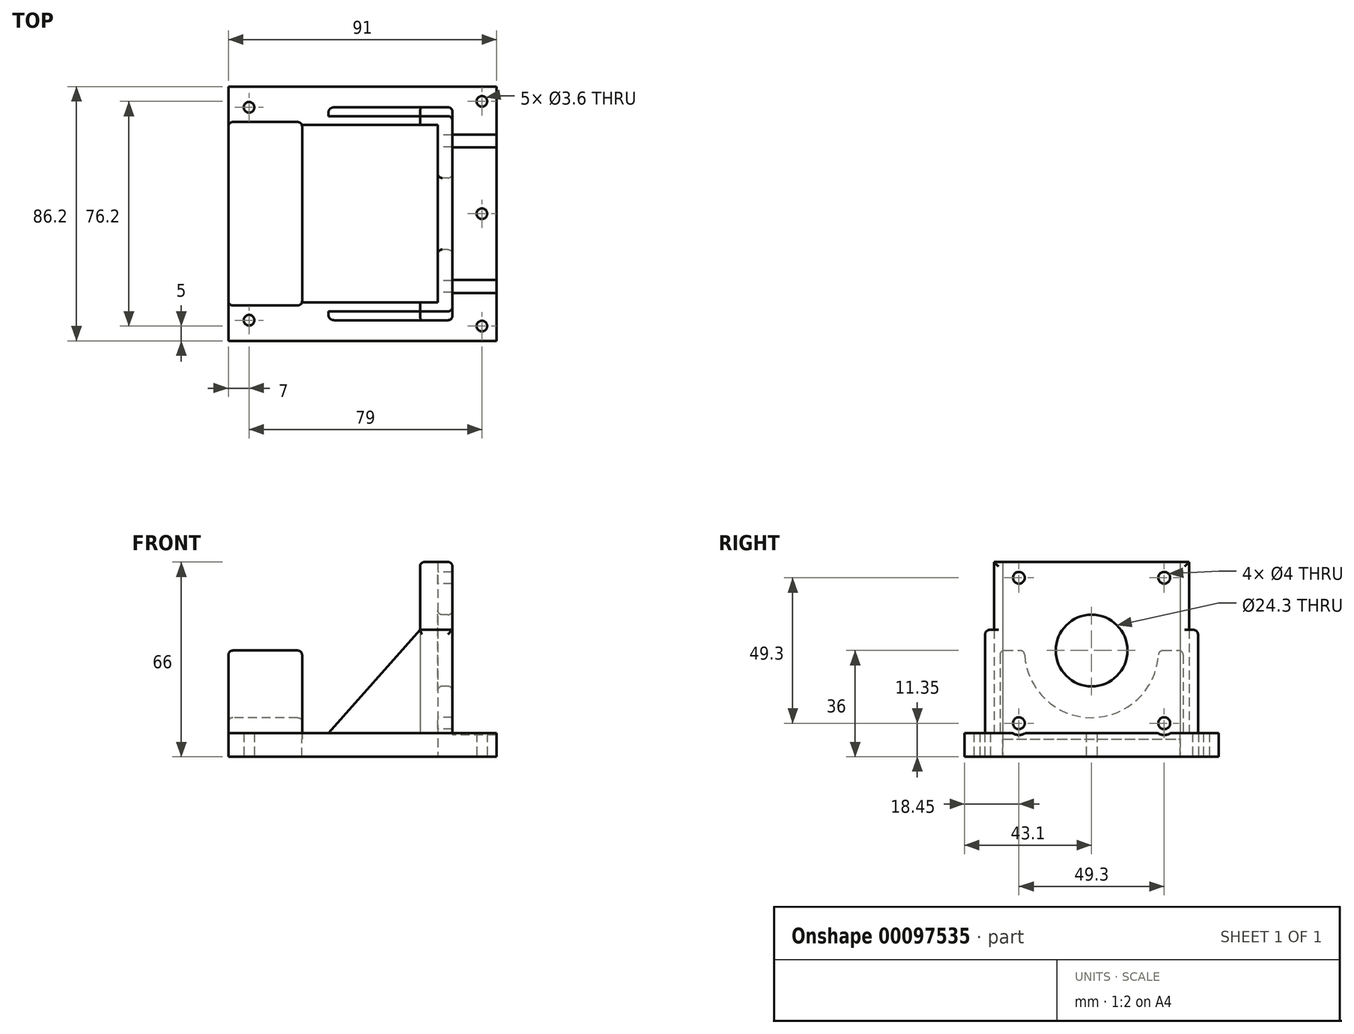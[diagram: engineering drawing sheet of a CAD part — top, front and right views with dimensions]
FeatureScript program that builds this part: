
annotation { "Feature Type Name" : "Feature", "Feature Type Description" : "" }
export const myFeature = defineFeature(function(context is Context, id is Id, definition is map)
    precondition{}
    {
        {
            var Q0;
            Q0=qCreatedBy(makeId("Right.planeOp"),FACE);
            var sketch = newSketch(context, id + "F0", { "sketchPlane" : qUnion([Q0])});
            skLineSegment(sketch, "E0.bottom", {"start": v(-30.1, 60) * mm, "end": v(30.1, 60) * mm});
            skLineSegment(sketch, "E0.top", {"start": v(-30.1, 0) * mm, "end": v(30.1, 0) * mm});
            skLineSegment(sketch, "E0.left", {"start": v(-30.1, 60) * mm, "end": v(-30.1, 0) * mm});
            skLineSegment(sketch, "E0.right", {"start": v(30.1, 60) * mm, "end": v(30.1, 0) * mm});
            skLineSegment(sketch, "E1.bottom", {"start": v(-33.1, 63) * mm, "end": v(33.1, 63) * mm});
            skLineSegment(sketch, "E1.top", {"start": v(-33.1, 0) * mm, "end": v(33.1, 0) * mm});
            skLineSegment(sketch, "E1.left", {"start": v(-33.1, 63) * mm, "end": v(-33.1, 0) * mm});
            skLineSegment(sketch, "E1.right", {"start": v(33.1, 63) * mm, "end": v(33.1, 0) * mm});
            skCircle(sketch, "E2", {"center": v(-24.65, 54.65) * mm, "radius": 2 * mm});
            skCircle(sketch, "E3", {"center": v(24.65, 54.65) * mm, "radius": 2 * mm});
            skCircle(sketch, "E4", {"center": v(24.65, 5.35) * mm, "radius": 2 * mm});
            skCircle(sketch, "E5", {"center": v(-24.65, 5.35) * mm, "radius": 2 * mm});
            skCircle(sketch, "E6", {"center": v(0, 30) * mm, "radius": 12.15 * mm});
            skSolve(sketch);
        }
        {
            var Q0;
            Q0=makeQuery(id+"F0.imprint","IMPRINT",FACE,{"disambiguationData":[TD([[makeQuery(id+"F0.imprint","IMPRINT",EDGE,{"derivedFrom":sQuery(id+"F0.wireOp",EDGE,"E0.bottom")}),1.0]])]});
            var Q1;
            Q1=makeQuery(id+"F0.imprint","IMPRINT",FACE,{"disambiguationData":[TD([[makeQuery(id+"F0.imprint","IMPRINT",EDGE,{"derivedFrom":sQuery(id+"F0.wireOp",EDGE,"E0.bottom")}),-1.0]])]});
            extrude(context, id + "F1", {"entities" : qUnion([Q0, Q1]), "depth" : 5 * mm});
        }
        {
            var Q0;
            Q0=makeQuery(id+"F0.imprint","IMPRINT",FACE,{"disambiguationData":[TD([[makeQuery(id+"F0.imprint","IMPRINT",EDGE,{"derivedFrom":sQuery(id+"F0.wireOp",EDGE,"E0.bottom")}),1.0]])]});
            extrude(context, id + "F2", {"entities" : qUnion([Q0]), "operationType" : NewBodyOperationType.ADD, "oppositeDirection" : true, "depth" : 6 * mm});
        }
        {
            var Q0;
            Q0=qCreatedBy(makeId("Top.planeOp"),FACE);
            var sketch = newSketch(context, id + "F3", { "sketchPlane" : qUnion([Q0])});
            skLineSegment(sketch, "E7.bottom", {"start": v(-6, -43.1) * mm, "end": v(20, -43.1) * mm});
            skLineSegment(sketch, "E7.top", {"start": v(-6, 43.1) * mm, "end": v(20, 43.1) * mm});
            skLineSegment(sketch, "E7.left", {"start": v(-6, -43.1) * mm, "end": v(-6, -30.1) * mm});
            skLineSegment(sketch, "E7.right", {"start": v(20, -43.1) * mm, "end": v(20, 43.1) * mm});
            skLineSegment(sketch, "E8.bottom", {"start": v(0, -30.1) * mm, "end": v(-6, -30.1) * mm});
            skLineSegment(sketch, "E8.top", {"start": v(0, 30.1) * mm, "end": v(-6, 30.1) * mm});
            skLineSegment(sketch, "E8.left", {"start": v(0, -30.1) * mm, "end": v(0, 30.1) * mm});
            skLineSegment(sketch, "E9.trimOffspring", {"start": v(-6, 30.1) * mm, "end": v(-6, 43.1) * mm});
            skCircle(sketch, "E10", {"center": v(15, -38.1) * mm, "radius": 1.8 * mm});
            skCircle(sketch, "E11", {"center": v(15, 38.1) * mm, "radius": 1.8 * mm});
            skCircle(sketch, "E12", {"center": v(15, 0) * mm, "radius": 1.8 * mm});
            skSolve(sketch);
        }
        {
            var Q0;
            Q0=makeQuery(id+"F3.imprint","IMPRINT",FACE,{"disambiguationData":[TD([[makeQuery(id+"F3.imprint","IMPRINT",EDGE,{"derivedFrom":sQuery(id+"F3.wireOp",EDGE,"E7.bottom")}),1.0]])]});
            extrude(context, id + "F4", {"entities" : qUnion([Q0]), "operationType" : NewBodyOperationType.ADD, "depth" : 2 * mm});
        }
        {
            var Q0;
            Q0=makeQuery(id+"F1.opExtrude","CAP_FACE",FACE,{"disambiguationData":[OSD([sQuery(id+"F0.wireOp",EDGE,"E1.bottom"),sQuery(id+"F0.wireOp",EDGE,"E1.top"),sQuery(id+"F0.wireOp",EDGE,"E1.left"),sQuery(id+"F0.wireOp",EDGE,"E1.right"),sQuery(id+"F0.wireOp",EDGE,"E2"),sQuery(id+"F0.wireOp",EDGE,"E3"),sQuery(id+"F0.wireOp",EDGE,"E4"),sQuery(id+"F0.wireOp",EDGE,"E5"),sQuery(id+"F0.wireOp",EDGE,"E6")])],"isStart":false});
            var sketch = newSketch(context, id + "F5", { "sketchPlane" : qUnion([Q0])});
            skCircle(sketch, "E13", {"center": v(-24.65, 5.35) * mm, "radius": 4 * mm});
            skCircle(sketch, "E14", {"center": v(24.65, 5.35) * mm, "radius": 4 * mm});
            skSolve(sketch);
        }
        {
            var Q0;
            {var subQ1=sQuery(id+"F0.wireOp",EDGE,"E5");Q0=makeQuery(id+"F5.imprint","IMPRINT",FACE,{"disambiguationData":[TD([[makeQuery(id+"F5.imprint","IMPRINT",EDGE,{"derivedFrom":makeQuery(id+"F1.opExtrude","CAP_EDGE",EDGE,{"disambiguationData":[OSD([subQ1])],"isStart":false})}),-1.0]])]});}
            var Q1;
            {var subQ0=sQuery(id+"F5.wireOp",EDGE,"E13");var subQ1=makeQuery(id+"F4.boolean.opBoolean","INTERSECT",EDGE,{"derivedFrom":[makeQuery(id+"F1.opExtrude","CAP_FACE",FACE,{"disambiguationData":[OSD([sQuery(id+"F0.wireOp",EDGE,"E1.bottom"),sQuery(id+"F0.wireOp",EDGE,"E1.top"),sQuery(id+"F0.wireOp",EDGE,"E1.left"),sQuery(id+"F0.wireOp",EDGE,"E1.right"),sQuery(id+"F0.wireOp",EDGE,"E2"),sQuery(id+"F0.wireOp",EDGE,"E3"),sQuery(id+"F0.wireOp",EDGE,"E4"),sQuery(id+"F0.wireOp",EDGE,"E5"),sQuery(id+"F0.wireOp",EDGE,"E6")])],"isStart":false}),makeQuery(id+"F4.opExtrude","CAP_FACE",FACE,{"disambiguationData":[OSD([sQuery(id+"F3.wireOp",EDGE,"E7.bottom"),sQuery(id+"F3.wireOp",EDGE,"E7.top"),sQuery(id+"F3.wireOp",EDGE,"E7.left"),sQuery(id+"F3.wireOp",EDGE,"E7.right"),sQuery(id+"F3.wireOp",EDGE,"E8.bottom"),sQuery(id+"F3.wireOp",EDGE,"E8.top"),sQuery(id+"F3.wireOp",EDGE,"E8.left"),sQuery(id+"F3.wireOp",EDGE,"E9.trimOffspring"),sQuery(id+"F3.wireOp",EDGE,"E10"),sQuery(id+"F3.wireOp",EDGE,"E11"),sQuery(id+"F3.wireOp",EDGE,"vc0lLMzM-xdFk-joIx-QcfE-IC59JL1JUAtQ"),sQuery(id+"F3.wireOp",EDGE,"XxfvqPpx-BB1E-VwMp-cwxA-6DKMUQReIGj5")])],"isStart":false})]});var subQ2=makeQuery(id+"F5.imprint","INTERSECT",VERTEX,{"disambiguationData":[OD(0.0)],"derivedFrom":[subQ1,subQ0]});Q1=makeQuery(id+"F5.imprint","IMPRINT",FACE,{"disambiguationData":[TD([[makeQuery(id+"F5.imprint","IMPRINT",EDGE,{"disambiguationData":[TD([[subQ2,-1.0]])],"derivedFrom":subQ0}),1.0]])]});}
            var Q2;
            {var subQ1=sQuery(id+"F0.wireOp",EDGE,"E4");Q2=makeQuery(id+"F5.imprint","IMPRINT",FACE,{"disambiguationData":[TD([[makeQuery(id+"F5.imprint","IMPRINT",EDGE,{"derivedFrom":makeQuery(id+"F1.opExtrude","CAP_EDGE",EDGE,{"disambiguationData":[OSD([subQ1])],"isStart":false})}),-1.0]])]});}
            var Q3;
            {var subQ0=sQuery(id+"F5.wireOp",EDGE,"E14");var subQ1=makeQuery(id+"F4.boolean.opBoolean","INTERSECT",EDGE,{"derivedFrom":[makeQuery(id+"F1.opExtrude","CAP_FACE",FACE,{"disambiguationData":[OSD([sQuery(id+"F0.wireOp",EDGE,"E1.bottom"),sQuery(id+"F0.wireOp",EDGE,"E1.top"),sQuery(id+"F0.wireOp",EDGE,"E1.left"),sQuery(id+"F0.wireOp",EDGE,"E1.right"),sQuery(id+"F0.wireOp",EDGE,"E2"),sQuery(id+"F0.wireOp",EDGE,"E3"),sQuery(id+"F0.wireOp",EDGE,"E4"),sQuery(id+"F0.wireOp",EDGE,"E5"),sQuery(id+"F0.wireOp",EDGE,"E6")])],"isStart":false}),makeQuery(id+"F4.opExtrude","CAP_FACE",FACE,{"disambiguationData":[OSD([sQuery(id+"F3.wireOp",EDGE,"E7.bottom"),sQuery(id+"F3.wireOp",EDGE,"E7.top"),sQuery(id+"F3.wireOp",EDGE,"E7.left"),sQuery(id+"F3.wireOp",EDGE,"E7.right"),sQuery(id+"F3.wireOp",EDGE,"E8.bottom"),sQuery(id+"F3.wireOp",EDGE,"E8.top"),sQuery(id+"F3.wireOp",EDGE,"E8.left"),sQuery(id+"F3.wireOp",EDGE,"E9.trimOffspring"),sQuery(id+"F3.wireOp",EDGE,"E10"),sQuery(id+"F3.wireOp",EDGE,"E11"),sQuery(id+"F3.wireOp",EDGE,"vc0lLMzM-xdFk-joIx-QcfE-IC59JL1JUAtQ"),sQuery(id+"F3.wireOp",EDGE,"XxfvqPpx-BB1E-VwMp-cwxA-6DKMUQReIGj5")])],"isStart":false})]});var subQ2=makeQuery(id+"F5.imprint","INTERSECT",VERTEX,{"disambiguationData":[OD(0.0)],"derivedFrom":[subQ1,subQ0]});Q3=makeQuery(id+"F5.imprint","IMPRINT",FACE,{"disambiguationData":[TD([[makeQuery(id+"F5.imprint","IMPRINT",EDGE,{"disambiguationData":[TD([[subQ2,1.0]])],"derivedFrom":subQ0}),1.0]])]});}
            var Q4;
            Q4=makeQuery(id+"F4.opExtrude","SWEPT_FACE",FACE,{"disambiguationData":[OSD([sQuery(id+"F3.wireOp",EDGE,"E7.right")])]});
            extrude(context, id + "F6", {"entities" : qUnion([Q0, Q1, Q2, Q3]), "operationType" : NewBodyOperationType.REMOVE, "endBound" : BoundingType.UP_TO_SURFACE, "endBoundEntityFace" : qUnion([Q4]), "depth" : 25 * mm});
        }
        {
            var Q0;
            Q0=qCreatedBy(makeId("Top.planeOp"),FACE);
            var sketch = newSketch(context, id + "F7", { "sketchPlane" : qUnion([Q0])});
            skLineSegment(sketch, "E15.bottom", {"start": v(-71, -43.1) * mm, "end": v(-6, -43.1) * mm});
            skLineSegment(sketch, "E15.top", {"start": v(-71, -30.1) * mm, "end": v(-6, -30.1) * mm});
            skLineSegment(sketch, "E15.left", {"start": v(-71, -43.1) * mm, "end": v(-71, -30.1) * mm});
            skLineSegment(sketch, "E15.right", {"start": v(-6, -43.1) * mm, "end": v(-6, -30.1) * mm});
            skLineSegment(sketch, "E16.bottom", {"start": v(-6, 30.1) * mm, "end": v(-71, 30.1) * mm});
            skLineSegment(sketch, "E16.top", {"start": v(-6, 43.1) * mm, "end": v(-71, 43.1) * mm});
            skLineSegment(sketch, "E16.left", {"start": v(-6, 30.1) * mm, "end": v(-6, 43.1) * mm});
            skLineSegment(sketch, "E16.right", {"start": v(-71, 30.1) * mm, "end": v(-71, 43.1) * mm});
            skCircle(sketch, "E17", {"center": v(-64, -36.1) * mm, "radius": 1.8 * mm});
            skCircle(sketch, "E18", {"center": v(-64, 36.1) * mm, "radius": 1.8 * mm});
            skSolve(sketch);
        }
        {
            var Q0;
            Q0=makeQuery(id+"F7.imprint","IMPRINT",FACE,{"disambiguationData":[TD([[makeQuery(id+"F7.imprint","IMPRINT",EDGE,{"derivedFrom":sQuery(id+"F7.wireOp",EDGE,"E15.bottom")}),1.0]])]});
            var Q1;
            Q1=makeQuery(id+"F7.imprint","IMPRINT",FACE,{"disambiguationData":[TD([[makeQuery(id+"F7.imprint","IMPRINT",EDGE,{"derivedFrom":sQuery(id+"F7.wireOp",EDGE,"E16.bottom")}),-1.0]])]});
            extrude(context, id + "F8", {"entities" : qUnion([Q0, Q1]), "operationType" : NewBodyOperationType.ADD, "depth" : 2 * mm});
        }
        {
            var Q0;
            Q0=qCreatedBy(makeId("Top.planeOp"),FACE);
            var sketch = newSketch(context, id + "F9", { "sketchPlane" : qUnion([Q0])});
            skLineSegment(sketch, "E19.bottom", {"start": v(-71, -31.1) * mm, "end": v(-46, -31.1) * mm});
            skLineSegment(sketch, "E19.top", {"start": v(-71, 31.1) * mm, "end": v(-46, 31.1) * mm});
            skLineSegment(sketch, "E19.left", {"start": v(-71, -31.1) * mm, "end": v(-71, 31.1) * mm});
            skLineSegment(sketch, "E19.right", {"start": v(-46, -31.1) * mm, "end": v(-46, 31.1) * mm});
            skSolve(sketch);
        }
        {
            var Q0;
            Q0=makeQuery(id+"F9.imprint","IMPRINT",FACE,{"disambiguationData":[TD([[makeQuery(id+"F9.imprint","IMPRINT",EDGE,{"derivedFrom":sQuery(id+"F9.wireOp",EDGE,"E19.bottom")}),1.0]])]});
            extrude(context, id + "F10", {"entities" : qUnion([Q0]), "operationType" : NewBodyOperationType.ADD, "depth" : 30 * mm});
        }
        {
            var Q0;
            Q0=makeQuery(id+"F10.boolean.opBoolean","MERGE",FACE,{"derivedFrom":[makeQuery(id+"F8.opExtrude","SWEPT_FACE",FACE,{"disambiguationData":[OSD([sQuery(id+"F7.wireOp",EDGE,"E15.left")])]}),makeQuery(id+"F8.opExtrude","SWEPT_FACE",FACE,{"disambiguationData":[OSD([sQuery(id+"F7.wireOp",EDGE,"E16.right")])]}),makeQuery(id+"F10.opExtrude","SWEPT_FACE",FACE,{"disambiguationData":[OSD([sQuery(id+"F9.wireOp",EDGE,"E19.left")])]})]});
            var sketch = newSketch(context, id + "F11", { "sketchPlane" : qUnion([Q0])});
            skCircle(sketch, "E20", {"center": v(0, 30) * mm, "radius": 22.75 * mm});
            skSolve(sketch);
        }
        {
            var Q0;
            {var subQ0=sQuery(id+"F11.wireOp",EDGE,"E20");var subQ1=makeQuery(id+"F10.opExtrude","CAP_EDGE",EDGE,{"disambiguationData":[OSD([sQuery(id+"F9.wireOp",EDGE,"E19.left")])],"isStart":false});var subQ2=makeQuery(id+"F11.imprint","INTERSECT",VERTEX,{"disambiguationData":[OD(0.0)],"derivedFrom":[subQ1,subQ0]});Q0=makeQuery(id+"F11.imprint","IMPRINT",FACE,{"disambiguationData":[TD([[makeQuery(id+"F11.imprint","IMPRINT",EDGE,{"disambiguationData":[TD([[subQ2,1.0]])],"derivedFrom":subQ0}),1.0]])]});}
            var Q1;
            {var subQ0=sQuery(id+"F11.wireOp",EDGE,"E20");var subQ1=makeQuery(id+"F10.opExtrude","CAP_EDGE",EDGE,{"disambiguationData":[OSD([sQuery(id+"F9.wireOp",EDGE,"E19.left")])],"isStart":false});var subQ2=makeQuery(id+"F11.imprint","INTERSECT",VERTEX,{"disambiguationData":[OD(0.0)],"derivedFrom":[subQ1,subQ0]});Q1=makeQuery(id+"F11.imprint","IMPRINT",FACE,{"disambiguationData":[TD([[makeQuery(id+"F11.imprint","IMPRINT",EDGE,{"disambiguationData":[TD([[subQ2,-1.0]])],"derivedFrom":subQ0}),1.0]])]});}
            var Q2;
            Q2=makeQuery(id+"F10.opExtrude","SWEPT_FACE",FACE,{"disambiguationData":[OSD([sQuery(id+"F9.wireOp",EDGE,"E19.right")])]});
            extrude(context, id + "F12", {"entities" : qUnion([Q0, Q1]), "operationType" : NewBodyOperationType.REMOVE, "endBound" : BoundingType.UP_TO_SURFACE, "oppositeDirection" : true, "endBoundEntityFace" : qUnion([Q2]), "depth" : 25 * mm});
        }
        {
            var Q0;
            Q0=qCreatedBy(makeId("Right.planeOp"),FACE);
            var sketch = newSketch(context, id + "F13", { "sketchPlane" : qUnion([Q0])});
            skLineSegment(sketch, "E21.bottom", {"start": v(-33.1, 68.2) * mm, "end": v(33.1, 68.2) * mm});
            skLineSegment(sketch, "E21.top", {"start": v(-33.1, 60) * mm, "end": v(33.1, 60) * mm});
            skLineSegment(sketch, "E21.left", {"start": v(-33.1, 68.2) * mm, "end": v(-33.1, 60) * mm});
            skLineSegment(sketch, "E21.right", {"start": v(33.1, 68.2) * mm, "end": v(33.1, 60) * mm});
            skSolve(sketch);
        }
        {
            var Q0;
            Q0=makeQuery(id+"F13.imprint","IMPRINT",FACE,{"disambiguationData":[TD([[makeQuery(id+"F13.imprint","IMPRINT",EDGE,{"derivedFrom":sQuery(id+"F13.wireOp",EDGE,"E21.bottom")}),-1.0]])]});
            extrude(context, id + "F14", {"entities" : qUnion([Q0]), "operationType" : NewBodyOperationType.REMOVE, "endBound" : BoundingType.SYMMETRIC, "oppositeDirection" : true, "depth" : 25 * mm});
        }
        {
            var Q0;
            {var subQ0=sQuery(id+"F0.wireOp",EDGE,"E1.right");Q0=makeQuery(id+"F2.boolean.opBoolean","MERGE",FACE,{"derivedFrom":[makeQuery(id+"F1.opExtrude","SWEPT_FACE",FACE,{"disambiguationData":[OSD([subQ0])]}),makeQuery(id+"F2.opExtrude","SWEPT_FACE",FACE,{"disambiguationData":[OSD([subQ0])]})]});}
            var sketch = newSketch(context, id + "F15", { "sketchPlane" : qUnion([Q0])});
            skLineSegment(sketch, "E22.bottom", {"start": v(-5, 2) * mm, "end": v(37, 2) * mm});
            skLineSegment(sketch, "E22.top", {"start": v(-5, 37) * mm, "end": v(6, 37) * mm});
            skLineSegment(sketch, "E22.left", {"start": v(-5, 2) * mm, "end": v(-5, 37) * mm});
            skLineSegment(sketch, "E23", {"start": v(6, 37) * mm, "end": v(37, 2) * mm});
            skSolve(sketch);
        }
        {
            var Q0;
            {var subQ3=sQuery(id+"F15.wireOp",EDGE,"E23");Q0=makeQuery(id+"F15.imprint","IMPRINT",FACE,{"disambiguationData":[TD([[makeQuery(id+"F15.imprint","IMPRINT",EDGE,{"derivedFrom":subQ3}),-1.0]])]});}
            var Q1;
            {var subQ4=sQuery(id+"F15.wireOp",EDGE,"E22.top");Q1=makeQuery(id+"F15.imprint","IMPRINT",FACE,{"disambiguationData":[TD([[makeQuery(id+"F15.imprint","IMPRINT",EDGE,{"derivedFrom":subQ4}),-1.0]])]});}
            extrude(context, id + "F16", {"entities" : qUnion([Q0, Q1]), "operationType" : NewBodyOperationType.ADD, "depth" : 3 * mm});
        }
        {
            var Q0;
            {var subQ0=sQuery(id+"F0.wireOp",EDGE,"E1.left");Q0=makeQuery(id+"F2.boolean.opBoolean","MERGE",FACE,{"derivedFrom":[makeQuery(id+"F1.opExtrude","SWEPT_FACE",FACE,{"disambiguationData":[OSD([subQ0])]}),makeQuery(id+"F2.opExtrude","SWEPT_FACE",FACE,{"disambiguationData":[OSD([subQ0])]})]});}
            var sketch = newSketch(context, id + "F17", { "sketchPlane" : qUnion([Q0])});
            skLineSegment(sketch, "E24.bottom", {"start": v(5, 2) * mm, "end": v(-37, 2) * mm});
            skLineSegment(sketch, "E24.top", {"start": v(5, 37) * mm, "end": v(-6, 37) * mm});
            skLineSegment(sketch, "E24.left", {"start": v(5, 2) * mm, "end": v(5, 37) * mm});
            skLineSegment(sketch, "E25", {"start": v(-6, 37) * mm, "end": v(-37, 2) * mm});
            skSolve(sketch);
        }
        {
            var Q0;
            {var subQ3=sQuery(id+"F17.wireOp",EDGE,"E25");Q0=makeQuery(id+"F17.imprint","IMPRINT",FACE,{"disambiguationData":[TD([[makeQuery(id+"F17.imprint","IMPRINT",EDGE,{"derivedFrom":subQ3}),1.0]])]});}
            var Q1;
            {var subQ4=sQuery(id+"F17.wireOp",EDGE,"E24.top");Q1=makeQuery(id+"F17.imprint","IMPRINT",FACE,{"disambiguationData":[TD([[makeQuery(id+"F17.imprint","IMPRINT",EDGE,{"derivedFrom":subQ4}),1.0]])]});}
            extrude(context, id + "F18", {"entities" : qUnion([Q0, Q1]), "operationType" : NewBodyOperationType.ADD, "depth" : 3 * mm});
        }
        {
            var Q0;
            {var subQ0=sQuery(id+"F0.wireOp",EDGE,"E4");var subQ1=sQuery(id+"F0.wireOp",EDGE,"E5");Q0=makeQuery(id+"F14.boolean.opBoolean","INTERSECT",EDGE,{"derivedFrom":[makeQuery(id+"F6.boolean.opBoolean","MERGE",FACE,{"derivedFrom":[makeQuery(id+"F1.opExtrude","CAP_FACE",FACE,{"disambiguationData":[OSD([sQuery(id+"F0.wireOp",EDGE,"E1.bottom"),sQuery(id+"F0.wireOp",EDGE,"E1.top"),sQuery(id+"F0.wireOp",EDGE,"E1.left"),sQuery(id+"F0.wireOp",EDGE,"E1.right"),sQuery(id+"F0.wireOp",EDGE,"E2"),sQuery(id+"F0.wireOp",EDGE,"E3"),subQ0,subQ1,sQuery(id+"F0.wireOp",EDGE,"E6")])],"isStart":false}),makeQuery(id+"F6.opExtrude","CAP_FACE",FACE,{"disambiguationData":[OSD([subQ1,sQuery(id+"F5.wireOp",EDGE,"E13")])],"isStart":true}),makeQuery(id+"F6.opExtrude","CAP_FACE",FACE,{"disambiguationData":[OSD([subQ0,sQuery(id+"F5.wireOp",EDGE,"E14")])],"isStart":true})]}),makeQuery(id+"F14.opExtrude","SWEPT_FACE",FACE,{"disambiguationData":[OSD([sQuery(id+"F13.wireOp",EDGE,"E21.top")])]})]});}
            var Q1;
            Q1=makeQuery(id+"F2.opExtrude","CAP_EDGE",EDGE,{"disambiguationData":[OSD([sQuery(id+"F0.wireOp",EDGE,"E0.bottom")])],"isStart":true});
            var Q2;
            Q2=makeQuery(id+"F2.opExtrude","SWEPT_EDGE",EDGE,{"disambiguationData":[OSD([sQuery(id+"F0.wireOp",EDGE,"E0.bottom"),sQuery(id+"F0.wireOp",EDGE,"E0.left")])]});
            var Q3;
            Q3=makeQuery(id+"F14.boolean.opBoolean","INTERSECT",EDGE,{"disambiguationData":[OD(0.0)],"derivedFrom":[makeQuery(id+"F4.boolean.opBoolean","MERGE",FACE,{"derivedFrom":[makeQuery(id+"F2.opExtrude","CAP_FACE",FACE,{"disambiguationData":[OSD([sQuery(id+"F0.wireOp",EDGE,"E0.bottom"),sQuery(id+"F0.wireOp",EDGE,"E0.left"),sQuery(id+"F0.wireOp",EDGE,"E0.right"),sQuery(id+"F0.wireOp",EDGE,"E1.bottom"),sQuery(id+"F0.wireOp",EDGE,"E1.top"),sQuery(id+"F0.wireOp",EDGE,"E1.left"),sQuery(id+"F0.wireOp",EDGE,"E1.right")])],"isStart":false}),makeQuery(id+"F4.opExtrude","SWEPT_FACE",FACE,{"disambiguationData":[OSD([sQuery(id+"F3.wireOp",EDGE,"E7.left")])]}),makeQuery(id+"F4.opExtrude","SWEPT_FACE",FACE,{"disambiguationData":[OSD([sQuery(id+"F3.wireOp",EDGE,"E9.trimOffspring")])]})]}),makeQuery(id+"F14.opExtrude","SWEPT_FACE",FACE,{"disambiguationData":[OSD([sQuery(id+"F13.wireOp",EDGE,"E21.top")])]})]});
            var Q4;
            Q4=makeQuery(id+"F2.opExtrude","SWEPT_EDGE",EDGE,{"disambiguationData":[OSD([sQuery(id+"F0.wireOp",EDGE,"E0.bottom"),sQuery(id+"F0.wireOp",EDGE,"E0.right")])]});
            var Q5;
            Q5=makeQuery(id+"F14.boolean.opBoolean","INTERSECT",EDGE,{"disambiguationData":[OD(1.0)],"derivedFrom":[makeQuery(id+"F4.boolean.opBoolean","MERGE",FACE,{"derivedFrom":[makeQuery(id+"F2.opExtrude","CAP_FACE",FACE,{"disambiguationData":[OSD([sQuery(id+"F0.wireOp",EDGE,"E0.bottom"),sQuery(id+"F0.wireOp",EDGE,"E0.left"),sQuery(id+"F0.wireOp",EDGE,"E0.right"),sQuery(id+"F0.wireOp",EDGE,"E1.bottom"),sQuery(id+"F0.wireOp",EDGE,"E1.top"),sQuery(id+"F0.wireOp",EDGE,"E1.left"),sQuery(id+"F0.wireOp",EDGE,"E1.right")])],"isStart":false}),makeQuery(id+"F4.opExtrude","SWEPT_FACE",FACE,{"disambiguationData":[OSD([sQuery(id+"F3.wireOp",EDGE,"E7.left")])]}),makeQuery(id+"F4.opExtrude","SWEPT_FACE",FACE,{"disambiguationData":[OSD([sQuery(id+"F3.wireOp",EDGE,"E9.trimOffspring")])]})]}),makeQuery(id+"F14.opExtrude","SWEPT_FACE",FACE,{"disambiguationData":[OSD([sQuery(id+"F13.wireOp",EDGE,"E21.top")])]})]});
            var Q6;
            Q6=makeQuery(id+"F14.boolean.opBoolean","COPY",EDGE,{"derivedFrom":makeQuery(id+"F14.opExtrude","SWEPT_EDGE",EDGE,{"disambiguationData":[OSD([sQuery(id+"F13.wireOp",EDGE,"E21.top"),sQuery(id+"F13.wireOp",EDGE,"E21.left")])]})});
            var Q7;
            Q7=makeQuery(id+"F14.boolean.opBoolean","COPY",EDGE,{"derivedFrom":makeQuery(id+"F14.opExtrude","SWEPT_EDGE",EDGE,{"disambiguationData":[OSD([sQuery(id+"F13.wireOp",EDGE,"E21.top"),sQuery(id+"F13.wireOp",EDGE,"E21.right")])]})});
            var Q8;
            Q8=makeQuery(id+"F12.boolean.opBoolean","COPY",FACE,{"derivedFrom":makeQuery(id+"F12.opExtrude","SWEPT_FACE",FACE,{"disambiguationData":[OSD([sQuery(id+"F11.wireOp",EDGE,"E20")])]})});
            var Q9;
            {var subQ0=sQuery(id+"F9.wireOp",EDGE,"E19.left");var subQ1=sQuery(id+"F9.wireOp",EDGE,"E19.bottom");var subQ2=sQuery(id+"F9.wireOp",EDGE,"E19.right");Q9=makeQuery(id+"F12.boolean.opBoolean","SPLIT",FACE,{"disambiguationData":[TD([makeQuery(id+"F10.opExtrude","SWEPT_FACE",FACE,{"disambiguationData":[OSD([subQ1])]})])],"derivedFrom":makeQuery(id+"F10.opExtrude","CAP_FACE",FACE,{"disambiguationData":[OSD([subQ1,sQuery(id+"F9.wireOp",EDGE,"E19.top"),subQ0,subQ2])],"isStart":false})});}
            var Q10;
            {var subQ0=sQuery(id+"F9.wireOp",EDGE,"E19.left");var subQ1=sQuery(id+"F9.wireOp",EDGE,"E19.top");var subQ2=sQuery(id+"F9.wireOp",EDGE,"E19.right");Q10=makeQuery(id+"F12.boolean.opBoolean","SPLIT",FACE,{"disambiguationData":[TD([makeQuery(id+"F10.opExtrude","SWEPT_FACE",FACE,{"disambiguationData":[OSD([subQ1])]})])],"derivedFrom":makeQuery(id+"F10.opExtrude","CAP_FACE",FACE,{"disambiguationData":[OSD([sQuery(id+"F9.wireOp",EDGE,"E19.bottom"),subQ1,subQ0,subQ2])],"isStart":false})});}
            var Q11;
            Q11=makeQuery(id+"F1.opExtrude","CAP_EDGE",EDGE,{"disambiguationData":[OSD([sQuery(id+"F0.wireOp",EDGE,"E6")])],"isStart":false});
            var Q12;
            Q12=makeQuery(id+"F1.opExtrude","CAP_EDGE",EDGE,{"disambiguationData":[OSD([sQuery(id+"F0.wireOp",EDGE,"E6")])],"isStart":true});
            var Q13;
            Q13=makeQuery(id+"F10.opExtrude","SWEPT_EDGE",EDGE,{"disambiguationData":[OSD([sQuery(id+"F9.wireOp",EDGE,"E19.top"),sQuery(id+"F9.wireOp",EDGE,"E19.left")])]});
            var Q14;
            Q14=makeQuery(id+"F10.opExtrude","SWEPT_EDGE",EDGE,{"disambiguationData":[OSD([sQuery(id+"F9.wireOp",EDGE,"E19.top"),sQuery(id+"F9.wireOp",EDGE,"E19.right")])]});
            var Q15;
            Q15=makeQuery(id+"F10.opExtrude","SWEPT_EDGE",EDGE,{"disambiguationData":[OSD([sQuery(id+"F9.wireOp",EDGE,"E19.bottom"),sQuery(id+"F9.wireOp",EDGE,"E19.right")])]});
            var Q16;
            Q16=makeQuery(id+"F10.opExtrude","SWEPT_EDGE",EDGE,{"disambiguationData":[OSD([sQuery(id+"F9.wireOp",EDGE,"E19.bottom"),sQuery(id+"F9.wireOp",EDGE,"E19.left")])]});
            var Q17;
            Q17=makeQuery(id+"F18.opExtrude","CAP_EDGE",EDGE,{"disambiguationData":[OSD([sQuery(id+"F17.wireOp",EDGE,"E25")])],"isStart":false});
            var Q18;
            Q18=makeQuery(id+"F18.opExtrude","CAP_EDGE",EDGE,{"disambiguationData":[OSD([sQuery(id+"F17.wireOp",EDGE,"E24.top")])],"isStart":false});
            var Q19;
            Q19=makeQuery(id+"F18.opExtrude","CAP_EDGE",EDGE,{"disambiguationData":[OSD([sQuery(id+"F17.wireOp",EDGE,"E24.left")])],"isStart":false});
            var Q20;
            Q20=makeQuery(id+"F16.opExtrude","CAP_EDGE",EDGE,{"disambiguationData":[OSD([sQuery(id+"F15.wireOp",EDGE,"E23")])],"isStart":false});
            var Q21;
            Q21=makeQuery(id+"F16.opExtrude","CAP_EDGE",EDGE,{"disambiguationData":[OSD([sQuery(id+"F15.wireOp",EDGE,"E22.top")])],"isStart":false});
            var Q22;
            Q22=makeQuery(id+"F16.opExtrude","CAP_EDGE",EDGE,{"disambiguationData":[OSD([sQuery(id+"F15.wireOp",EDGE,"E22.left")])],"isStart":false});
            var Q23;
            Q23=makeQuery(id+"F1.opExtrude","CAP_EDGE",EDGE,{"disambiguationData":[OSD([sQuery(id+"F0.wireOp",EDGE,"E1.right")])],"isStart":false});
            var Q24;
            Q24=makeQuery(id+"F1.opExtrude","CAP_EDGE",EDGE,{"disambiguationData":[OSD([sQuery(id+"F0.wireOp",EDGE,"E1.left")])],"isStart":false});
            fillet(context, id + "F19", {"entities" : qUnion([Q0, Q1, Q2, Q3, Q4, Q5, Q6, Q7, Q8, Q9, Q10, Q11, Q12, Q13, Q14, Q15, Q16, Q17, Q18, Q19, Q20, Q21, Q22, Q23, Q24]), "radius" : 1.5 * mm, "tangentPropagation" : true, "allowEdgeOverflow" : false});
        }
        {
            var Q0;
            {var subQ0=sQuery(id+"F0.wireOp",EDGE,"E1.top");Q0=makeQuery(id+"F10.boolean.opBoolean","MERGE",FACE,{"derivedFrom":[makeQuery(id+"F8.boolean.opBoolean","MERGE",FACE,{"derivedFrom":[makeQuery(id+"F4.boolean.opBoolean","MERGE",FACE,{"derivedFrom":[makeQuery(id+"F2.boolean.opBoolean","MERGE",FACE,{"derivedFrom":[makeQuery(id+"F1.opExtrude","SWEPT_FACE",FACE,{"disambiguationData":[OSD([subQ0])]}),makeQuery(id+"F2.opExtrude","SWEPT_FACE",FACE,{"disambiguationData":[OSD([subQ0]),TDD([makeQuery(id+"F0.imprint","IMPRINT",EDGE,{"disambiguationData":[TD([[makeQuery(id+"F0.imprint","INTERSECT",VERTEX,{"derivedFrom":[sQuery(id+"F0.wireOp",EDGE,"E0.left"),subQ0]}),1.0]])],"derivedFrom":subQ0})])]}),makeQuery(id+"F2.opExtrude","SWEPT_FACE",FACE,{"disambiguationData":[OSD([subQ0]),TDD([makeQuery(id+"F0.imprint","IMPRINT",EDGE,{"disambiguationData":[TD([[makeQuery(id+"F0.imprint","INTERSECT",VERTEX,{"derivedFrom":[sQuery(id+"F0.wireOp",EDGE,"E0.right"),subQ0]}),-1.0]])],"derivedFrom":subQ0})])]})]}),makeQuery(id+"F4.opExtrude","CAP_FACE",FACE,{"disambiguationData":[OSD([sQuery(id+"F3.wireOp",EDGE,"E7.bottom"),sQuery(id+"F3.wireOp",EDGE,"E7.top"),sQuery(id+"F3.wireOp",EDGE,"E7.left"),sQuery(id+"F3.wireOp",EDGE,"E7.right"),sQuery(id+"F3.wireOp",EDGE,"E8.bottom"),sQuery(id+"F3.wireOp",EDGE,"E8.top"),sQuery(id+"F3.wireOp",EDGE,"E8.left"),sQuery(id+"F3.wireOp",EDGE,"E9.trimOffspring"),sQuery(id+"F3.wireOp",EDGE,"E10"),sQuery(id+"F3.wireOp",EDGE,"E11"),sQuery(id+"F3.wireOp",EDGE,"E12")])],"isStart":true})]}),makeQuery(id+"F8.opExtrude","CAP_FACE",FACE,{"disambiguationData":[OSD([sQuery(id+"F7.wireOp",EDGE,"E15.bottom"),sQuery(id+"F7.wireOp",EDGE,"E15.top"),sQuery(id+"F7.wireOp",EDGE,"E15.left"),sQuery(id+"F7.wireOp",EDGE,"E15.right"),sQuery(id+"F7.wireOp",EDGE,"E17")])],"isStart":true}),makeQuery(id+"F8.opExtrude","CAP_FACE",FACE,{"disambiguationData":[OSD([sQuery(id+"F7.wireOp",EDGE,"E16.bottom"),sQuery(id+"F7.wireOp",EDGE,"E16.top"),sQuery(id+"F7.wireOp",EDGE,"E16.left"),sQuery(id+"F7.wireOp",EDGE,"E16.right"),sQuery(id+"F7.wireOp",EDGE,"E18")])],"isStart":true})]}),makeQuery(id+"F10.opExtrude","CAP_FACE",FACE,{"disambiguationData":[OSD([sQuery(id+"F9.wireOp",EDGE,"E19.bottom"),sQuery(id+"F9.wireOp",EDGE,"E19.top"),sQuery(id+"F9.wireOp",EDGE,"E19.left"),sQuery(id+"F9.wireOp",EDGE,"E19.right")])],"isStart":true})]});}
            var sketch = newSketch(context, id + "F20", { "sketchPlane" : qUnion([Q0])});
            skLineSegment(sketch, "E26.bottom", {"start": v(-71, 43.1) * mm, "end": v(20, 43.1) * mm});
            skLineSegment(sketch, "E26.top", {"start": v(-71, -43.1) * mm, "end": v(20, -43.1) * mm});
            skLineSegment(sketch, "E26.left", {"start": v(-71, 43.1) * mm, "end": v(-71, -43.1) * mm});
            skLineSegment(sketch, "E26.right", {"start": v(20, 43.1) * mm, "end": v(20, -43.1) * mm});
            skCircle(sketch, "E27", {"center": v(-64, 36.1) * mm, "radius": 1.8 * mm});
            skCircle(sketch, "E28", {"center": v(-64, -36.1) * mm, "radius": 1.8 * mm});
            skCircle(sketch, "E29", {"center": v(15, 0) * mm, "radius": 1.8 * mm});
            skCircle(sketch, "E30", {"center": v(15, 38.1) * mm, "radius": 1.8 * mm});
            skCircle(sketch, "E31", {"center": v(15, -38.1) * mm, "radius": 1.8 * mm});
            skLineSegment(sketch, "E32.bottom", {"start": v(-46.09, 30.1) * mm, "end": v(0, 30.1) * mm});
            skLineSegment(sketch, "E32.top", {"start": v(-46.09, -30.1) * mm, "end": v(0, -30.1) * mm});
            skLineSegment(sketch, "E32.left", {"start": v(-46.09, 30.1) * mm, "end": v(-46.09, -30.1) * mm});
            skLineSegment(sketch, "E32.right", {"start": v(0, 30.1) * mm, "end": v(0, -30.1) * mm});
            skSolve(sketch);
        }
        {
            var Q0;
            Q0=makeQuery(id+"F20.imprint","IMPRINT",FACE,{"disambiguationData":[TD([[makeQuery(id+"F20.imprint","IMPRINT",EDGE,{"derivedFrom":sQuery(id+"F20.wireOp",EDGE,"E26.bottom")}),-1.0]])]});
            extrude(context, id + "F21", {"entities" : qUnion([Q0]), "operationType" : NewBodyOperationType.ADD, "depth" : 6 * mm});
        }
    });
